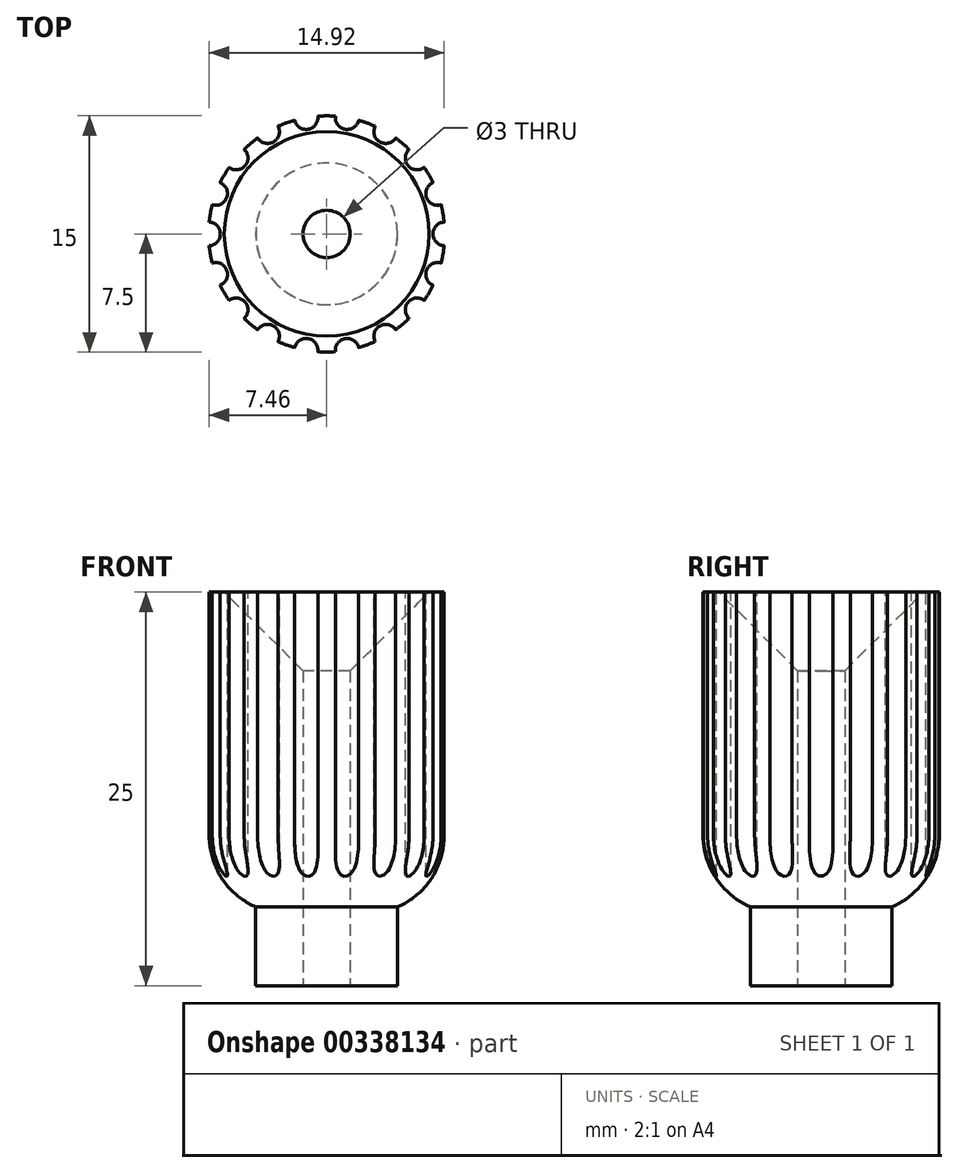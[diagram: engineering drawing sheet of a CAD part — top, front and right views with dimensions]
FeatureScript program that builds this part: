
annotation { "Feature Type Name" : "Feature", "Feature Type Description" : "" }
export const myFeature = defineFeature(function(context is Context, id is Id, definition is map)
    precondition{}
    {
        {
            var Q0;
            Q0=qCreatedBy(makeId("Top.planeOp"),FACE);
            var sketch = newSketch(context, id + "F0", { "sketchPlane" : qUnion([Q0])});
            skCircle(sketch, "E0", {"center": v(0, 0) * mm, "radius": 1.5 * mm});
            skCircle(sketch, "E1", {"center": v(0, 0) * mm, "radius": 4.5 * mm});
            skSolve(sketch);
        }
        {
            var Q0;
            Q0 = qSketchRegion(id + "F0", true);
            extrude(context, id + "F1", {"entities" : qUnion([Q0]), "depth" : 5 * mm});
        }
        {
            var Q0;
            Q0=makeQuery(id+"F1.opExtrude","CAP_FACE",FACE,{"disambiguationData":[OSD([sQuery(id+"F0.wireOp",EDGE,"E0"),sQuery(id+"F0.wireOp",EDGE,"E1")])],"isStart":false});
            var sketch = newSketch(context, id + "F2", { "sketchPlane" : qUnion([Q0])});
            skCircle(sketch, "E2", {"center": v(0, 0) * mm, "radius": 7.5 * mm});
            skCircle(sketch, "E3", {"center": v(0, 0) * mm, "radius": 1.5 * mm});
            skSolve(sketch);
        }
        {
            var Q0;
            Q0 = qSketchRegion(id + "F2", true);
            extrude(context, id + "F3", {"entities" : qUnion([Q0]), "operationType" : NewBodyOperationType.ADD, "depth" : 20 * mm});
        }
        {
            var Q0;
            Q0=makeQuery(id+"F3.opExtrude","CAP_EDGE",EDGE,{"disambiguationData":[OSD([sQuery(id+"F2.wireOp",EDGE,"E2")])],"isStart":true});
            fillet(context, id + "F4", {"entities" : qUnion([Q0]), "radius" : 5 * mm, "tangentPropagation" : true, "allowEdgeOverflow" : false});
        }
        {
            var Q0;
            Q0=makeQuery(id+"F3.opExtrude","CAP_EDGE",EDGE,{"disambiguationData":[OSD([sQuery(id+"F2.wireOp",EDGE,"E3")])],"isStart":false});
            chamfer(context, id + "F5", {"entities" : qUnion([Q0]), "width" : 5 * mm, "tangentPropagation" : true});
        }
        {
            var Q0;
            Q0=makeQuery(id+"F3.opExtrude","CAP_FACE",FACE,{"disambiguationData":[OSD([sQuery(id+"F2.wireOp",EDGE,"E2"),sQuery(id+"F2.wireOp",EDGE,"E3")])],"isStart":false});
            var sketch = newSketch(context, id + "F6", { "sketchPlane" : qUnion([Q0])});
            skCircle(sketch, "E4", {"center": v(-7.5, 0) * mm, "radius": 0.75 * mm});
            skCircle(sketch, "E5.1.0", {"center": v(-7.05, -2.57) * mm, "radius": 0.75 * mm});
            skCircle(sketch, "E5.2.0", {"center": v(-5.75, -4.82) * mm, "radius": 0.75 * mm});
            skCircle(sketch, "E5.3.0", {"center": v(-3.75, -6.5) * mm, "radius": 0.75 * mm});
            skCircle(sketch, "E5.4.0", {"center": v(-1.3, -7.39) * mm, "radius": 0.75 * mm});
            skCircle(sketch, "E5.5.0", {"center": v(1.3, -7.39) * mm, "radius": 0.75 * mm});
            skCircle(sketch, "E5.6.0", {"center": v(3.75, -6.5) * mm, "radius": 0.75 * mm});
            skCircle(sketch, "E5.7.0", {"center": v(5.75, -4.82) * mm, "radius": 0.75 * mm});
            skCircle(sketch, "E5.8.0", {"center": v(7.05, -2.57) * mm, "radius": 0.75 * mm});
            skCircle(sketch, "E5.9.0", {"center": v(7.5, 0) * mm, "radius": 0.75 * mm});
            skCircle(sketch, "E5.10.0", {"center": v(7.05, 2.57) * mm, "radius": 0.75 * mm});
            skCircle(sketch, "E5.11.0", {"center": v(5.75, 4.82) * mm, "radius": 0.75 * mm});
            skCircle(sketch, "E5.12.0", {"center": v(3.75, 6.5) * mm, "radius": 0.75 * mm});
            skCircle(sketch, "E5.13.0", {"center": v(1.3, 7.39) * mm, "radius": 0.75 * mm});
            skCircle(sketch, "E5.14.0", {"center": v(-1.3, 7.39) * mm, "radius": 0.75 * mm});
            skCircle(sketch, "E5.15.0", {"center": v(-3.75, 6.5) * mm, "radius": 0.75 * mm});
            skCircle(sketch, "E5.16.0", {"center": v(-5.75, 4.82) * mm, "radius": 0.75 * mm});
            skCircle(sketch, "E5.17.0", {"center": v(-7.05, 2.57) * mm, "radius": 0.75 * mm});
            skPoint(sketch, "E5.center", {"position": v(0, 0) * mm});
            skSolve(sketch);
        }
        {
            var Q0;
            {var subQ0=sQuery(id+"F6.wireOp",EDGE,"E5.17.0");var subQ1=makeQuery(id+"F3.opExtrude","CAP_EDGE",EDGE,{"disambiguationData":[OSD([sQuery(id+"F2.wireOp",EDGE,"E2")])],"isStart":false});var subQ2=makeQuery(id+"F6.imprint","INTERSECT",VERTEX,{"disambiguationData":[OD(0.0)],"derivedFrom":[subQ1,subQ0]});Q0=makeQuery(id+"F6.imprint","IMPRINT",FACE,{"disambiguationData":[TD([[makeQuery(id+"F6.imprint","IMPRINT",EDGE,{"disambiguationData":[TD([[subQ2,-1.0]])],"derivedFrom":subQ0}),1.0]])]});}
            var Q1;
            {var subQ0=sQuery(id+"F6.wireOp",EDGE,"E5.16.0");var subQ1=makeQuery(id+"F3.opExtrude","CAP_EDGE",EDGE,{"disambiguationData":[OSD([sQuery(id+"F2.wireOp",EDGE,"E2")])],"isStart":false});var subQ2=makeQuery(id+"F6.imprint","INTERSECT",VERTEX,{"disambiguationData":[OD(0.0)],"derivedFrom":[subQ1,subQ0]});Q1=makeQuery(id+"F6.imprint","IMPRINT",FACE,{"disambiguationData":[TD([[makeQuery(id+"F6.imprint","IMPRINT",EDGE,{"disambiguationData":[TD([[subQ2,-1.0]])],"derivedFrom":subQ0}),1.0]])]});}
            var Q2;
            {var subQ0=sQuery(id+"F6.wireOp",EDGE,"E5.15.0");var subQ1=makeQuery(id+"F3.opExtrude","CAP_EDGE",EDGE,{"disambiguationData":[OSD([sQuery(id+"F2.wireOp",EDGE,"E2")])],"isStart":false});var subQ2=makeQuery(id+"F6.imprint","INTERSECT",VERTEX,{"disambiguationData":[OD(0.0)],"derivedFrom":[subQ1,subQ0]});Q2=makeQuery(id+"F6.imprint","IMPRINT",FACE,{"disambiguationData":[TD([[makeQuery(id+"F6.imprint","IMPRINT",EDGE,{"disambiguationData":[TD([[subQ2,-1.0]])],"derivedFrom":subQ0}),1.0]])]});}
            var Q3;
            {var subQ0=sQuery(id+"F6.wireOp",EDGE,"E5.14.0");var subQ1=makeQuery(id+"F3.opExtrude","CAP_EDGE",EDGE,{"disambiguationData":[OSD([sQuery(id+"F2.wireOp",EDGE,"E2")])],"isStart":false});var subQ2=makeQuery(id+"F6.imprint","INTERSECT",VERTEX,{"disambiguationData":[OD(0.0)],"derivedFrom":[subQ1,subQ0]});Q3=makeQuery(id+"F6.imprint","IMPRINT",FACE,{"disambiguationData":[TD([[makeQuery(id+"F6.imprint","IMPRINT",EDGE,{"disambiguationData":[TD([[subQ2,-1.0]])],"derivedFrom":subQ0}),1.0]])]});}
            var Q4;
            {var subQ0=sQuery(id+"F6.wireOp",EDGE,"E5.13.0");var subQ1=makeQuery(id+"F3.opExtrude","CAP_EDGE",EDGE,{"disambiguationData":[OSD([sQuery(id+"F2.wireOp",EDGE,"E2")])],"isStart":false});var subQ2=makeQuery(id+"F6.imprint","INTERSECT",VERTEX,{"disambiguationData":[OD(0.0)],"derivedFrom":[subQ1,subQ0]});Q4=makeQuery(id+"F6.imprint","IMPRINT",FACE,{"disambiguationData":[TD([[makeQuery(id+"F6.imprint","IMPRINT",EDGE,{"disambiguationData":[TD([[subQ2,-1.0]])],"derivedFrom":subQ0}),1.0]])]});}
            var Q5;
            {var subQ0=sQuery(id+"F6.wireOp",EDGE,"E5.12.0");var subQ1=makeQuery(id+"F3.opExtrude","CAP_EDGE",EDGE,{"disambiguationData":[OSD([sQuery(id+"F2.wireOp",EDGE,"E2")])],"isStart":false});var subQ2=makeQuery(id+"F6.imprint","INTERSECT",VERTEX,{"disambiguationData":[OD(0.0)],"derivedFrom":[subQ1,subQ0]});Q5=makeQuery(id+"F6.imprint","IMPRINT",FACE,{"disambiguationData":[TD([[makeQuery(id+"F6.imprint","IMPRINT",EDGE,{"disambiguationData":[TD([[subQ2,-1.0]])],"derivedFrom":subQ0}),1.0]])]});}
            var Q6;
            {var subQ0=sQuery(id+"F6.wireOp",EDGE,"E5.11.0");var subQ1=makeQuery(id+"F3.opExtrude","CAP_EDGE",EDGE,{"disambiguationData":[OSD([sQuery(id+"F2.wireOp",EDGE,"E2")])],"isStart":false});var subQ2=makeQuery(id+"F6.imprint","INTERSECT",VERTEX,{"disambiguationData":[OD(0.0)],"derivedFrom":[subQ1,subQ0]});Q6=makeQuery(id+"F6.imprint","IMPRINT",FACE,{"disambiguationData":[TD([[makeQuery(id+"F6.imprint","IMPRINT",EDGE,{"disambiguationData":[TD([[subQ2,-1.0]])],"derivedFrom":subQ0}),1.0]])]});}
            var Q7;
            {var subQ0=sQuery(id+"F6.wireOp",EDGE,"E5.10.0");var subQ1=makeQuery(id+"F3.opExtrude","CAP_EDGE",EDGE,{"disambiguationData":[OSD([sQuery(id+"F2.wireOp",EDGE,"E2")])],"isStart":false});var subQ2=makeQuery(id+"F6.imprint","INTERSECT",VERTEX,{"disambiguationData":[OD(0.0)],"derivedFrom":[subQ1,subQ0]});Q7=makeQuery(id+"F6.imprint","IMPRINT",FACE,{"disambiguationData":[TD([[makeQuery(id+"F6.imprint","IMPRINT",EDGE,{"disambiguationData":[TD([[subQ2,1.0]])],"derivedFrom":subQ0}),1.0]])]});}
            var Q8;
            {var subQ0=sQuery(id+"F6.wireOp",EDGE,"E4");var subQ1=makeQuery(id+"F3.opExtrude","CAP_EDGE",EDGE,{"disambiguationData":[OSD([sQuery(id+"F2.wireOp",EDGE,"E2")])],"isStart":false});var subQ2=makeQuery(id+"F6.imprint","INTERSECT",VERTEX,{"disambiguationData":[OD(0.0)],"derivedFrom":[subQ1,subQ0]});Q8=makeQuery(id+"F6.imprint","IMPRINT",FACE,{"disambiguationData":[TD([[makeQuery(id+"F6.imprint","IMPRINT",EDGE,{"disambiguationData":[TD([[subQ2,-1.0]])],"derivedFrom":subQ0}),1.0]])]});}
            var Q9;
            {var subQ0=sQuery(id+"F6.wireOp",EDGE,"E5.1.0");var subQ1=makeQuery(id+"F3.opExtrude","CAP_EDGE",EDGE,{"disambiguationData":[OSD([sQuery(id+"F2.wireOp",EDGE,"E2")])],"isStart":false});var subQ2=makeQuery(id+"F6.imprint","INTERSECT",VERTEX,{"disambiguationData":[OD(0.0)],"derivedFrom":[subQ1,subQ0]});Q9=makeQuery(id+"F6.imprint","IMPRINT",FACE,{"disambiguationData":[TD([[makeQuery(id+"F6.imprint","IMPRINT",EDGE,{"disambiguationData":[TD([[subQ2,-1.0]])],"derivedFrom":subQ0}),1.0]])]});}
            var Q10;
            {var subQ0=sQuery(id+"F6.wireOp",EDGE,"E5.2.0");var subQ1=makeQuery(id+"F3.opExtrude","CAP_EDGE",EDGE,{"disambiguationData":[OSD([sQuery(id+"F2.wireOp",EDGE,"E2")])],"isStart":false});var subQ2=makeQuery(id+"F6.imprint","INTERSECT",VERTEX,{"disambiguationData":[OD(0.0)],"derivedFrom":[subQ1,subQ0]});Q10=makeQuery(id+"F6.imprint","IMPRINT",FACE,{"disambiguationData":[TD([[makeQuery(id+"F6.imprint","IMPRINT",EDGE,{"disambiguationData":[TD([[subQ2,1.0]])],"derivedFrom":subQ0}),1.0]])]});}
            var Q11;
            {var subQ0=sQuery(id+"F6.wireOp",EDGE,"E5.3.0");var subQ1=makeQuery(id+"F3.opExtrude","CAP_EDGE",EDGE,{"disambiguationData":[OSD([sQuery(id+"F2.wireOp",EDGE,"E2")])],"isStart":false});var subQ2=makeQuery(id+"F6.imprint","INTERSECT",VERTEX,{"disambiguationData":[OD(0.0)],"derivedFrom":[subQ1,subQ0]});Q11=makeQuery(id+"F6.imprint","IMPRINT",FACE,{"disambiguationData":[TD([[makeQuery(id+"F6.imprint","IMPRINT",EDGE,{"disambiguationData":[TD([[subQ2,1.0]])],"derivedFrom":subQ0}),1.0]])]});}
            var Q12;
            {var subQ0=sQuery(id+"F6.wireOp",EDGE,"E5.4.0");var subQ1=makeQuery(id+"F3.opExtrude","CAP_EDGE",EDGE,{"disambiguationData":[OSD([sQuery(id+"F2.wireOp",EDGE,"E2")])],"isStart":false});var subQ2=makeQuery(id+"F6.imprint","INTERSECT",VERTEX,{"disambiguationData":[OD(0.0)],"derivedFrom":[subQ1,subQ0]});Q12=makeQuery(id+"F6.imprint","IMPRINT",FACE,{"disambiguationData":[TD([[makeQuery(id+"F6.imprint","IMPRINT",EDGE,{"disambiguationData":[TD([[subQ2,1.0]])],"derivedFrom":subQ0}),1.0]])]});}
            var Q13;
            {var subQ0=sQuery(id+"F6.wireOp",EDGE,"E5.5.0");var subQ1=makeQuery(id+"F3.opExtrude","CAP_EDGE",EDGE,{"disambiguationData":[OSD([sQuery(id+"F2.wireOp",EDGE,"E2")])],"isStart":false});var subQ2=makeQuery(id+"F6.imprint","INTERSECT",VERTEX,{"disambiguationData":[OD(0.0)],"derivedFrom":[subQ1,subQ0]});Q13=makeQuery(id+"F6.imprint","IMPRINT",FACE,{"disambiguationData":[TD([[makeQuery(id+"F6.imprint","IMPRINT",EDGE,{"disambiguationData":[TD([[subQ2,1.0]])],"derivedFrom":subQ0}),1.0]])]});}
            var Q14;
            {var subQ0=sQuery(id+"F6.wireOp",EDGE,"E5.6.0");var subQ1=makeQuery(id+"F3.opExtrude","CAP_EDGE",EDGE,{"disambiguationData":[OSD([sQuery(id+"F2.wireOp",EDGE,"E2")])],"isStart":false});var subQ2=makeQuery(id+"F6.imprint","INTERSECT",VERTEX,{"disambiguationData":[OD(0.0)],"derivedFrom":[subQ1,subQ0]});Q14=makeQuery(id+"F6.imprint","IMPRINT",FACE,{"disambiguationData":[TD([[makeQuery(id+"F6.imprint","IMPRINT",EDGE,{"disambiguationData":[TD([[subQ2,1.0]])],"derivedFrom":subQ0}),1.0]])]});}
            var Q15;
            {var subQ0=sQuery(id+"F6.wireOp",EDGE,"E5.7.0");var subQ1=makeQuery(id+"F3.opExtrude","CAP_EDGE",EDGE,{"disambiguationData":[OSD([sQuery(id+"F2.wireOp",EDGE,"E2")])],"isStart":false});var subQ2=makeQuery(id+"F6.imprint","INTERSECT",VERTEX,{"disambiguationData":[OD(0.0)],"derivedFrom":[subQ1,subQ0]});Q15=makeQuery(id+"F6.imprint","IMPRINT",FACE,{"disambiguationData":[TD([[makeQuery(id+"F6.imprint","IMPRINT",EDGE,{"disambiguationData":[TD([[subQ2,1.0]])],"derivedFrom":subQ0}),1.0]])]});}
            var Q16;
            {var subQ0=sQuery(id+"F6.wireOp",EDGE,"E5.8.0");var subQ1=makeQuery(id+"F3.opExtrude","CAP_EDGE",EDGE,{"disambiguationData":[OSD([sQuery(id+"F2.wireOp",EDGE,"E2")])],"isStart":false});var subQ2=makeQuery(id+"F6.imprint","INTERSECT",VERTEX,{"disambiguationData":[OD(0.0)],"derivedFrom":[subQ1,subQ0]});Q16=makeQuery(id+"F6.imprint","IMPRINT",FACE,{"disambiguationData":[TD([[makeQuery(id+"F6.imprint","IMPRINT",EDGE,{"disambiguationData":[TD([[subQ2,1.0]])],"derivedFrom":subQ0}),1.0]])]});}
            var Q17;
            {var subQ0=sQuery(id+"F6.wireOp",EDGE,"E5.9.0");var subQ1=makeQuery(id+"F3.opExtrude","CAP_EDGE",EDGE,{"disambiguationData":[OSD([sQuery(id+"F2.wireOp",EDGE,"E2")])],"isStart":false});var subQ2=makeQuery(id+"F6.imprint","INTERSECT",VERTEX,{"disambiguationData":[OD(0.0)],"derivedFrom":[subQ1,subQ0]});Q17=makeQuery(id+"F6.imprint","IMPRINT",FACE,{"disambiguationData":[TD([[makeQuery(id+"F6.imprint","IMPRINT",EDGE,{"disambiguationData":[TD([[subQ2,1.0]])],"derivedFrom":subQ0}),1.0]])]});}
            extrude(context, id + "F7", {"entities" : qUnion([Q0, Q1, Q2, Q3, Q4, Q5, Q6, Q7, Q8, Q9, Q10, Q11, Q12, Q13, Q14, Q15, Q16, Q17]), "operationType" : NewBodyOperationType.REMOVE, "oppositeDirection" : true, "offsetDistance" : 25 * mm, "depth" : 25 * mm});
        }
    });
